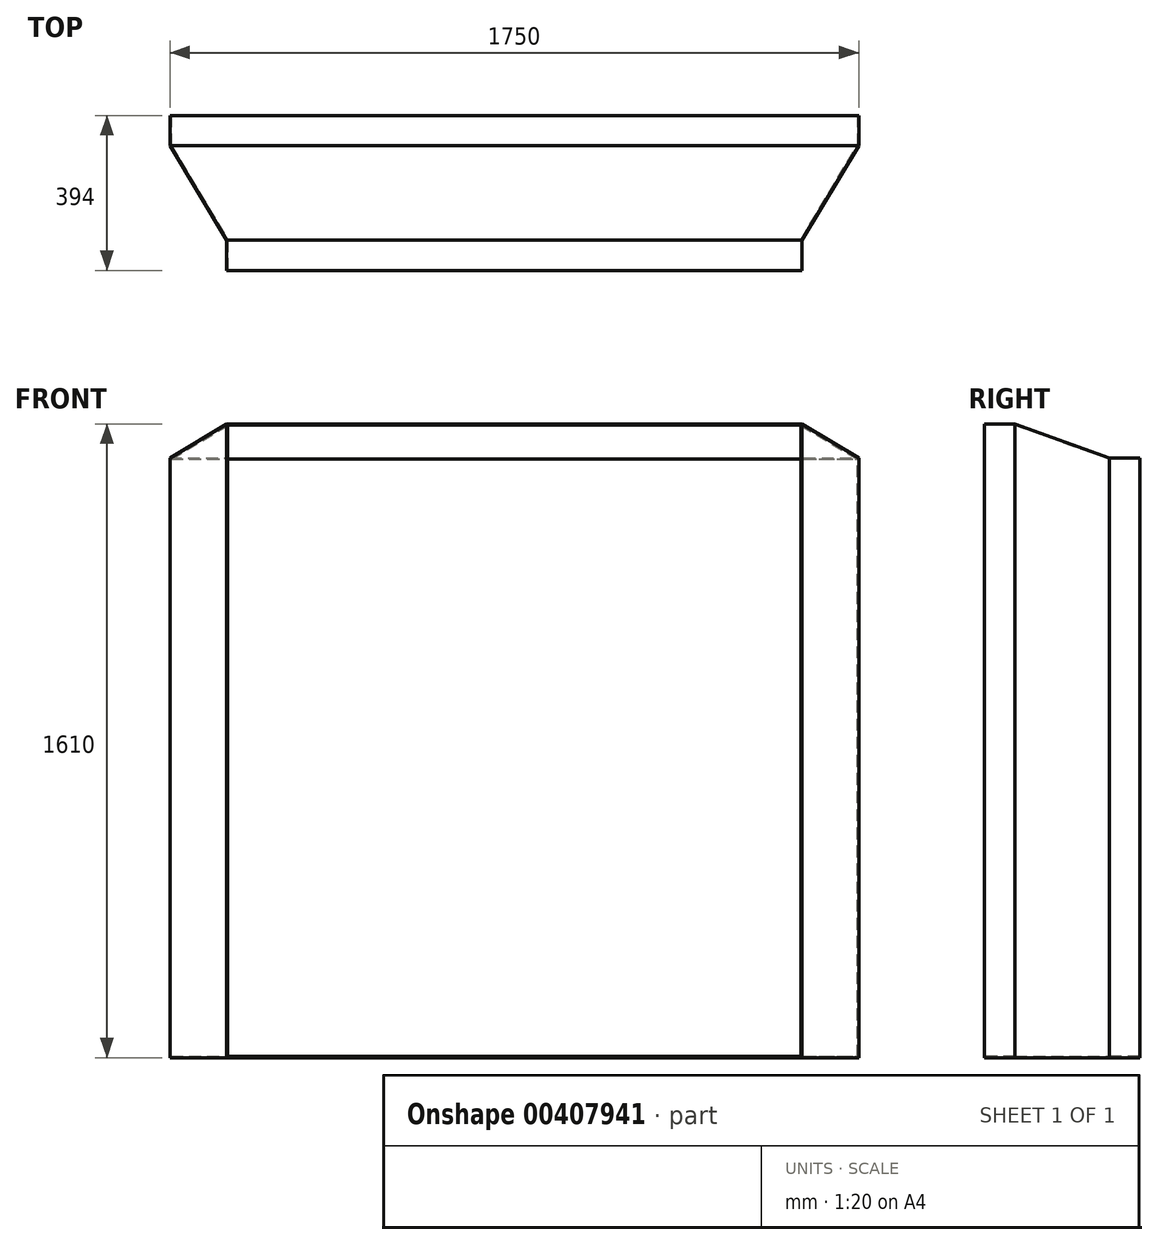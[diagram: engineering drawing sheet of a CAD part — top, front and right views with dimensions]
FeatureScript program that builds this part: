
annotation { "Feature Type Name" : "Feature", "Feature Type Description" : "" }
export const myFeature = defineFeature(function(context is Context, id is Id, definition is map)
    precondition{}
    {
        {
            var Q0;
            Q0=qCreatedBy(makeId("Front.planeOp"),FACE);
            var sketch = newSketch(context, id + "F0", { "sketchPlane" : qUnion([Q0])});
            skLineSegment(sketch, "E0.bottom", {"start": v(-731, 1610) * mm, "end": v(731, 1610) * mm});
            skLineSegment(sketch, "E0.top", {"start": v(-731, 0) * mm, "end": v(731, 0) * mm});
            skLineSegment(sketch, "E0.left", {"start": v(-731, 1610) * mm, "end": v(-731, 0) * mm});
            skLineSegment(sketch, "E0.right", {"start": v(731, 1610) * mm, "end": v(731, 0) * mm});
            skSolve(sketch);
        }
        {
            var Q0;
            Q0=makeQuery(id+"F0.imprint","IMPRINT",FACE,{"disambiguationData":[TD([[makeQuery(id+"F0.imprint","IMPRINT",EDGE,{"derivedFrom":sQuery(id+"F0.wireOp",EDGE,"E0.bottom")}),-1.0]])]});
            extrude(context, id + "F1", {"entities" : qUnion([Q0]), "oppositeDirection" : true, "depth" : (80 - 3) * mm});
        }
        {
            var Q0;
            Q0=makeQuery(id+"F1.opExtrude","CAP_FACE",FACE,{"disambiguationData":[OSD([sQuery(id+"F0.wireOp",EDGE,"E0.bottom"),sQuery(id+"F0.wireOp",EDGE,"E0.top"),sQuery(id+"F0.wireOp",EDGE,"E0.left"),sQuery(id+"F0.wireOp",EDGE,"E0.right")])],"isStart":false});
            cPlane(context, id + "F2", {"entities" : qUnion([Q0]), "cplaneType" : CPlaneType.OFFSET, "offset" : 240 * mm, "width" : 150 * mm, "height" : 150 * mm});
        }
        {
            var Q0;
            Q0=qCreatedBy(id+"F2.planeOp",FACE);
            var sketch = newSketch(context, id + "F3", { "sketchPlane" : qUnion([Q0])});
            skLineSegment(sketch, "E1.bottom", {"start": v(875, 0) * mm, "end": v(-875, 0) * mm});
            skLineSegment(sketch, "E1.top", {"start": v(875, 1524) * mm, "end": v(-875, 1524) * mm});
            skLineSegment(sketch, "E1.left", {"start": v(875, 0) * mm, "end": v(875, 1524) * mm});
            skLineSegment(sketch, "E1.right", {"start": v(-875, 0) * mm, "end": v(-875, 1524) * mm});
            skSolve(sketch);
        }
        {
            var Q0;
            Q0 = qSketchRegion(id + "F3", true);
            extrude(context, id + "F4", {"entities" : qUnion([Q0]), "depth" : (80 - 3) * mm});
        }
        {
            var Q0;
            Q0=makeQuery(id+"F1.opExtrude","CAP_FACE",FACE,{"disambiguationData":[OSD([sQuery(id+"F0.wireOp",EDGE,"E0.bottom"),sQuery(id+"F0.wireOp",EDGE,"E0.top"),sQuery(id+"F0.wireOp",EDGE,"E0.left"),sQuery(id+"F0.wireOp",EDGE,"E0.right")])],"isStart":false});
            var Q1;
            Q1=makeQuery(id+"F4.opExtrude","CAP_FACE",FACE,{"disambiguationData":[OSD([sQuery(id+"F3.wireOp",EDGE,"E1.bottom"),sQuery(id+"F3.wireOp",EDGE,"E1.top"),sQuery(id+"F3.wireOp",EDGE,"E1.left"),sQuery(id+"F3.wireOp",EDGE,"E1.right")])],"isStart":true});
            loft(context, id + "F5", {"operationType" : NewBodyOperationType.ADD, "sheetProfilesArray" : [{ "sheetProfileEntities" : qUnion([Q0]) }, { "sheetProfileEntities" : qUnion([Q1]) }]});
        }
        {
            var Q0;
            Q0=makeQuery(id+"F1.opExtrude","CAP_FACE",FACE,{"disambiguationData":[OSD([sQuery(id+"F0.wireOp",EDGE,"E0.bottom"),sQuery(id+"F0.wireOp",EDGE,"E0.top"),sQuery(id+"F0.wireOp",EDGE,"E0.left"),sQuery(id+"F0.wireOp",EDGE,"E0.right")])],"isStart":true});
            var Q1;
            Q1=makeQuery(id+"F4.opExtrude","CAP_FACE",FACE,{"disambiguationData":[OSD([sQuery(id+"F3.wireOp",EDGE,"E1.bottom"),sQuery(id+"F3.wireOp",EDGE,"E1.top"),sQuery(id+"F3.wireOp",EDGE,"E1.left"),sQuery(id+"F3.wireOp",EDGE,"E1.right")])],"isStart":false});
            shell(context, id + "F6", {"entities" : qUnion([Q0, Q1]), "thickness" : 3 * mm});
        }
    });
